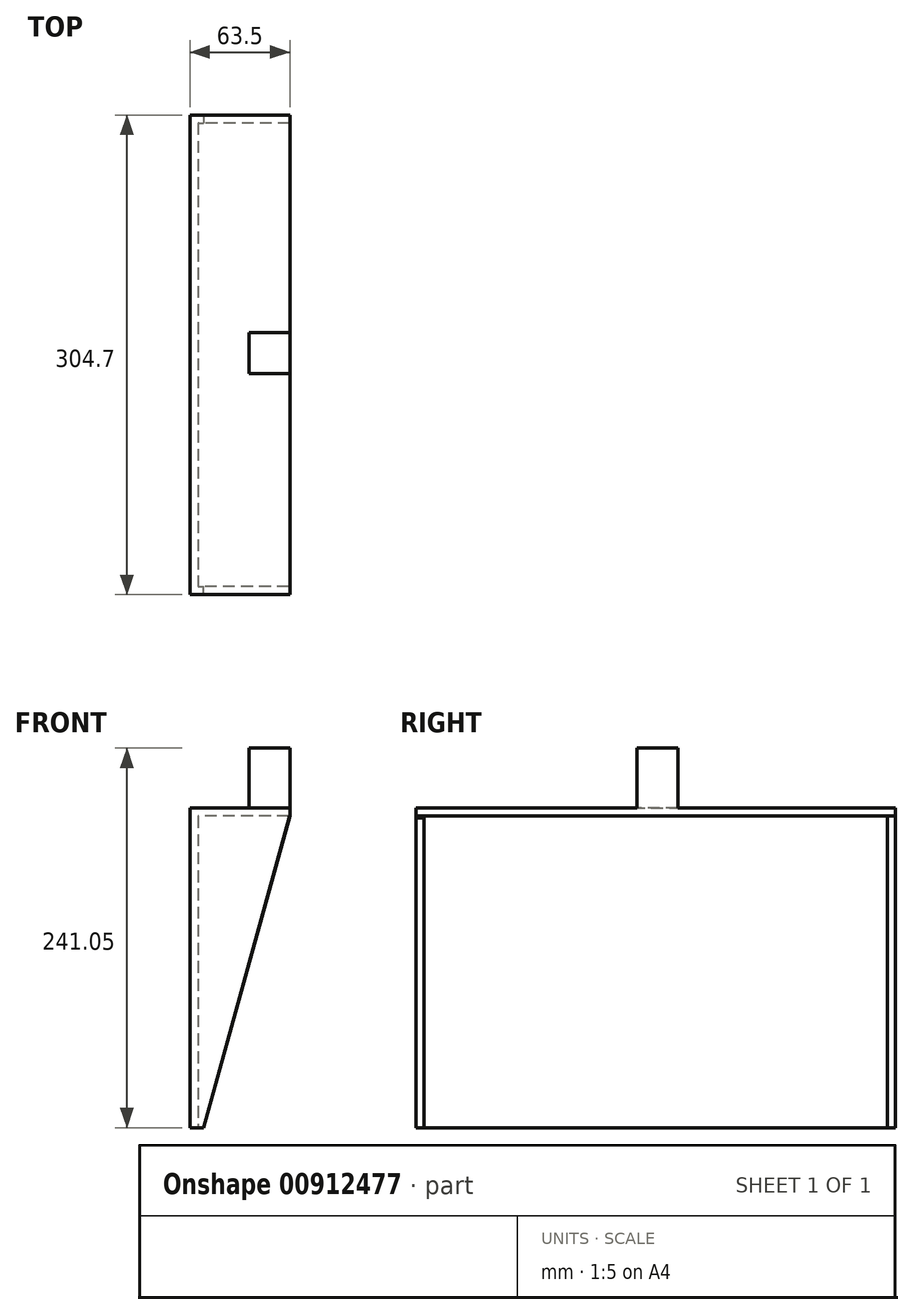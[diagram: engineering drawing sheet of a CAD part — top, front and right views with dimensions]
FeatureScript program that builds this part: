
annotation { "Feature Type Name" : "Feature", "Feature Type Description" : "" }
export const myFeature = defineFeature(function(context is Context, id is Id, definition is map)
    precondition{}
    {
        {
            var Q0;
            Q0=qCreatedBy(makeId("Right.planeOp"),FACE);
            var sketch = newSketch(context, id + "F0", { "sketchPlane" : qUnion([Q0])});
            skLineSegment(sketch, "E0.bottom", {"start": v(-161.87, 90.65) * mm, "end": v(142.83, 90.65) * mm});
            skLineSegment(sketch, "E0.top", {"start": v(-161.87, -112.3) * mm, "end": v(142.83, -112.3) * mm});
            skLineSegment(sketch, "E0.left", {"start": v(-161.87, 90.65) * mm, "end": v(-161.87, -112.3) * mm});
            skLineSegment(sketch, "E0.right", {"start": v(142.83, 90.65) * mm, "end": v(142.83, -112.3) * mm});
            skSolve(sketch);
        }
        {
            var Q0;
            Q0=makeQuery(id+"F0.imprint","IMPRINT",FACE,{"disambiguationData":[TD([[makeQuery(id+"F0.imprint","IMPRINT",EDGE,{"derivedFrom":sQuery(id+"F0.wireOp",EDGE,"E0.bottom")}),-1.0]])]});
            extrude(context, id + "F1", {"entities" : qUnion([Q0]), "depth" : 63.5 * mm, "offsetDistance" : 25.4 * mm});
        }
        {
            var Q0;
            Q0=makeQuery(id+"F1.opExtrude","CAP_FACE",FACE,{"disambiguationData":[OSD([sQuery(id+"F0.wireOp",EDGE,"E0.bottom"),sQuery(id+"F0.wireOp",EDGE,"E0.top"),sQuery(id+"F0.wireOp",EDGE,"E0.left"),sQuery(id+"F0.wireOp",EDGE,"E0.right")])],"isStart":false});
            shell(context, id + "F2", {"entities" : qUnion([Q0]), "thickness" : 5.08 * mm});
        }
        {
            var Q0;
            Q0=makeQuery(id+"F1.opExtrude","SWEPT_FACE",FACE,{"disambiguationData":[OSD([sQuery(id+"F0.wireOp",EDGE,"E0.top")])]});
            extrude(context, id + "F3", {"entities" : qUnion([Q0]), "operationType" : NewBodyOperationType.REMOVE, "oppositeDirection" : true, "depth" : 25.4 * mm, "offsetDistance" : 25.4 * mm});
        }
        {
            var Q0;
            Q0=makeQuery(id+"F3.boolean.opBoolean","COPY",FACE,{"derivedFrom":makeQuery(id+"F3.opExtrude","CAP_FACE",FACE,{"disambiguationData":[OSD([sQuery(id+"F0.wireOp",EDGE,"E0.top")])],"isStart":false})});
            extrude(context, id + "F4", {"entities" : qUnion([Q0]), "operationType" : NewBodyOperationType.ADD, "depth" : 25.4 * mm, "offsetDistance" : 25.4 * mm});
        }
        {
            var Q0;
            {var subQ0=sQuery(id+"F0.wireOp",EDGE,"E0.top");var subQ1=sQuery(id+"F0.wireOp",EDGE,"E0.left");var subQ2=makeQuery(id+"F2.opShell","OFFSET_FACE",FACE,{"disambiguationData":[OSD([subQ1])]});Q0=makeQuery(id+"F4.boolean.opBoolean","MERGE",FACE,{"derivedFrom":[subQ2,makeQuery(id+"F4.opExtrude","SWEPT_FACE",FACE,{"disambiguationData":[OSD([subQ0,subQ1]),TDD([makeQuery(id+"F3.boolean.opBoolean","INTERSECT",EDGE,{"derivedFrom":[subQ2,makeQuery(id+"F3.opExtrude","CAP_FACE",FACE,{"disambiguationData":[OSD([subQ0])],"isStart":false})]})])]})]});}
            var sketch = newSketch(context, id + "F5", { "sketchPlane" : qUnion([Q0])});
            skSolve(sketch);
        }
        {
            var Q0;
            {var subQ0=sQuery(id+"F0.wireOp",EDGE,"E0.top");var subQ1=sQuery(id+"F0.wireOp",EDGE,"E0.right");var subQ2=makeQuery(id+"F2.opShell","OFFSET_FACE",FACE,{"disambiguationData":[OSD([subQ1])]});Q0=makeQuery(id+"F4.boolean.opBoolean","MERGE",FACE,{"derivedFrom":[subQ2,makeQuery(id+"F4.opExtrude","SWEPT_FACE",FACE,{"disambiguationData":[OSD([subQ0,subQ1]),TDD([makeQuery(id+"F3.boolean.opBoolean","INTERSECT",EDGE,{"derivedFrom":[subQ2,makeQuery(id+"F3.opExtrude","CAP_FACE",FACE,{"disambiguationData":[OSD([subQ0])],"isStart":false})]})])]})]});}
            var sketch = newSketch(context, id + "F6", { "sketchPlane" : qUnion([Q0])});
            skLineSegment(sketch, "E1", {"start": v(63.5, 85.57) * mm, "end": v(8.69, -112.3) * mm});
            skLineSegment(sketch, "E2", {"start": v(63.5, 85.57) * mm, "end": v(63.5, -112.3) * mm});
            skLineSegment(sketch, "E3", {"start": v(63.5, -112.3) * mm, "end": v(8.69, -112.3) * mm});
            skSolve(sketch);
        }
        {
            var Q0;
            Q0 = qSketchRegion(id + "F6", true);
            extrude(context, id + "F7", {"entities" : qUnion([Q0]), "operationType" : NewBodyOperationType.REMOVE, "oppositeDirection" : true, "depth" : 123.95 * mm, "offsetDistance" : 25.4 * mm});
        }
        {
            var Q0;
            {var subQ0=sQuery(id+"F0.wireOp",EDGE,"E0.left");var subQ1=sQuery(id+"F0.wireOp",EDGE,"E0.bottom");Q0=makeQuery(id+"F5.imprint","IMPRINT",FACE,{"disambiguationData":[TD([[makeQuery(id+"F5.imprint","IMPRINT",EDGE,{"derivedFrom":makeQuery(id+"F2.opShell","OFFSET_EDGE",EDGE,{"disambiguationData":[OSD([subQ1,subQ0])]})}),-1.0]])]});}
            var sketch = newSketch(context, id + "F8", { "sketchPlane" : qUnion([Q0])});
            skLineSegment(sketch, "E4", {"start": v(-63.13, 84.87) * mm, "end": v(-8.4, -112.94) * mm});
            skLineSegment(sketch, "E5", {"start": v(-63.13, 84.87) * mm, "end": v(-63.13, -112.94) * mm});
            skLineSegment(sketch, "E6", {"start": v(-63.13, -112.94) * mm, "end": v(-8.4, -112.94) * mm});
            skLineSegment(sketch, "E7", {"start": v(-63.13, -112.94) * mm, "end": v(-58.9, -107.47) * mm});
            skSolve(sketch);
        }
        {
            var Q0;
            Q0 = qSketchRegion(id + "F8", true);
            extrude(context, id + "F9", {"entities" : qUnion([Q0]), "operationType" : NewBodyOperationType.REMOVE, "oppositeDirection" : true, "depth" : 25.4 * mm, "offsetDistance" : 25.4 * mm});
        }
        {
            var Q0;
            {var subQ0=sQuery(id+"F0.wireOp",EDGE,"E0.right");var subQ1=sQuery(id+"F0.wireOp",EDGE,"E0.left");var subQ2=sQuery(id+"F0.wireOp",EDGE,"E0.top");var subQ3=makeQuery(id+"F1.opExtrude","CAP_FACE",FACE,{"disambiguationData":[OSD([sQuery(id+"F0.wireOp",EDGE,"E0.bottom"),subQ2,subQ1,subQ0])],"isStart":false});var subQ5=makeQuery(id+"F3.opExtrude","CAP_EDGE",EDGE,{"disambiguationData":[OSD([subQ2]),TDD([makeQuery(id+"F1.opExtrude","CAP_EDGE",EDGE,{"disambiguationData":[OSD([subQ2])],"isStart":false})])],"isStart":false});Q0=makeQuery(id+"F4.boolean.opBoolean","MERGE",FACE,{"derivedFrom":[subQ3,makeQuery(id+"F4.opExtrude","SWEPT_FACE",FACE,{"disambiguationData":[OSD([subQ2]),TDD([makeQuery(id+"F3.boolean.opBoolean","COPY",EDGE,{"disambiguationData":[TD([makeQuery(id+"F1.opExtrude","SWEPT_FACE",FACE,{"disambiguationData":[OSD([subQ1])]})])],"derivedFrom":subQ5})])]}),makeQuery(id+"F4.opExtrude","SWEPT_FACE",FACE,{"disambiguationData":[OSD([subQ2]),TDD([makeQuery(id+"F3.boolean.opBoolean","COPY",EDGE,{"disambiguationData":[TD([makeQuery(id+"F1.opExtrude","SWEPT_FACE",FACE,{"disambiguationData":[OSD([subQ0])]})])],"derivedFrom":subQ5})])]})]});}
            var sketch = newSketch(context, id + "F10", { "sketchPlane" : qUnion([Q0])});
            skLineSegment(sketch, "E8.bottom", {"start": v(-161.87, 85.57) * mm, "end": v(-156.79, 85.57) * mm});
            skLineSegment(sketch, "E8.top", {"start": v(-161.87, -112.3) * mm, "end": v(-156.79, -112.3) * mm});
            skLineSegment(sketch, "E8.left", {"start": v(-161.87, 85.57) * mm, "end": v(-161.87, -112.3) * mm});
            skLineSegment(sketch, "E8.right", {"start": v(-156.79, 85.57) * mm, "end": v(-156.79, -112.3) * mm});
            skSolve(sketch);
        }
        {
            var Q0;
            Q0 = qSketchRegion(id + "F10", true);
            extrude(context, id + "F11", {"entities" : qUnion([Q0]), "operationType" : NewBodyOperationType.REMOVE, "oppositeDirection" : true, "depth" : 0.5 * mm, "offsetDistance" : 25.4 * mm});
        }
        {
            var Q0;
            Q0=makeQuery(id+"F1.opExtrude","SWEPT_FACE",FACE,{"disambiguationData":[OSD([sQuery(id+"F0.wireOp",EDGE,"E0.bottom")])]});
            var sketch = newSketch(context, id + "F12", { "sketchPlane" : qUnion([Q0])});
            skLineSegment(sketch, "E9.bottom", {"start": v(63.5, 4.48) * mm, "end": v(37.67, 4.48) * mm});
            skLineSegment(sketch, "E9.top", {"start": v(63.5, -21.3) * mm, "end": v(37.67, -21.3) * mm});
            skLineSegment(sketch, "E9.left", {"start": v(63.5, 4.48) * mm, "end": v(63.5, -21.3) * mm});
            skLineSegment(sketch, "E9.right", {"start": v(37.67, 4.48) * mm, "end": v(37.67, -21.3) * mm});
            skSolve(sketch);
        }
        {
            var Q0;
            Q0=makeQuery(id+"F12.imprint","IMPRINT",FACE,{"disambiguationData":[TD([[makeQuery(id+"F12.imprint","IMPRINT",EDGE,{"derivedFrom":sQuery(id+"F12.wireOp",EDGE,"E9.bottom")}),1.0]])]});
            extrude(context, id + "F13", {"entities" : qUnion([Q0]), "operationType" : NewBodyOperationType.ADD, "depth" : 38.1 * mm, "offsetDistance" : 25.4 * mm});
        }
    });
